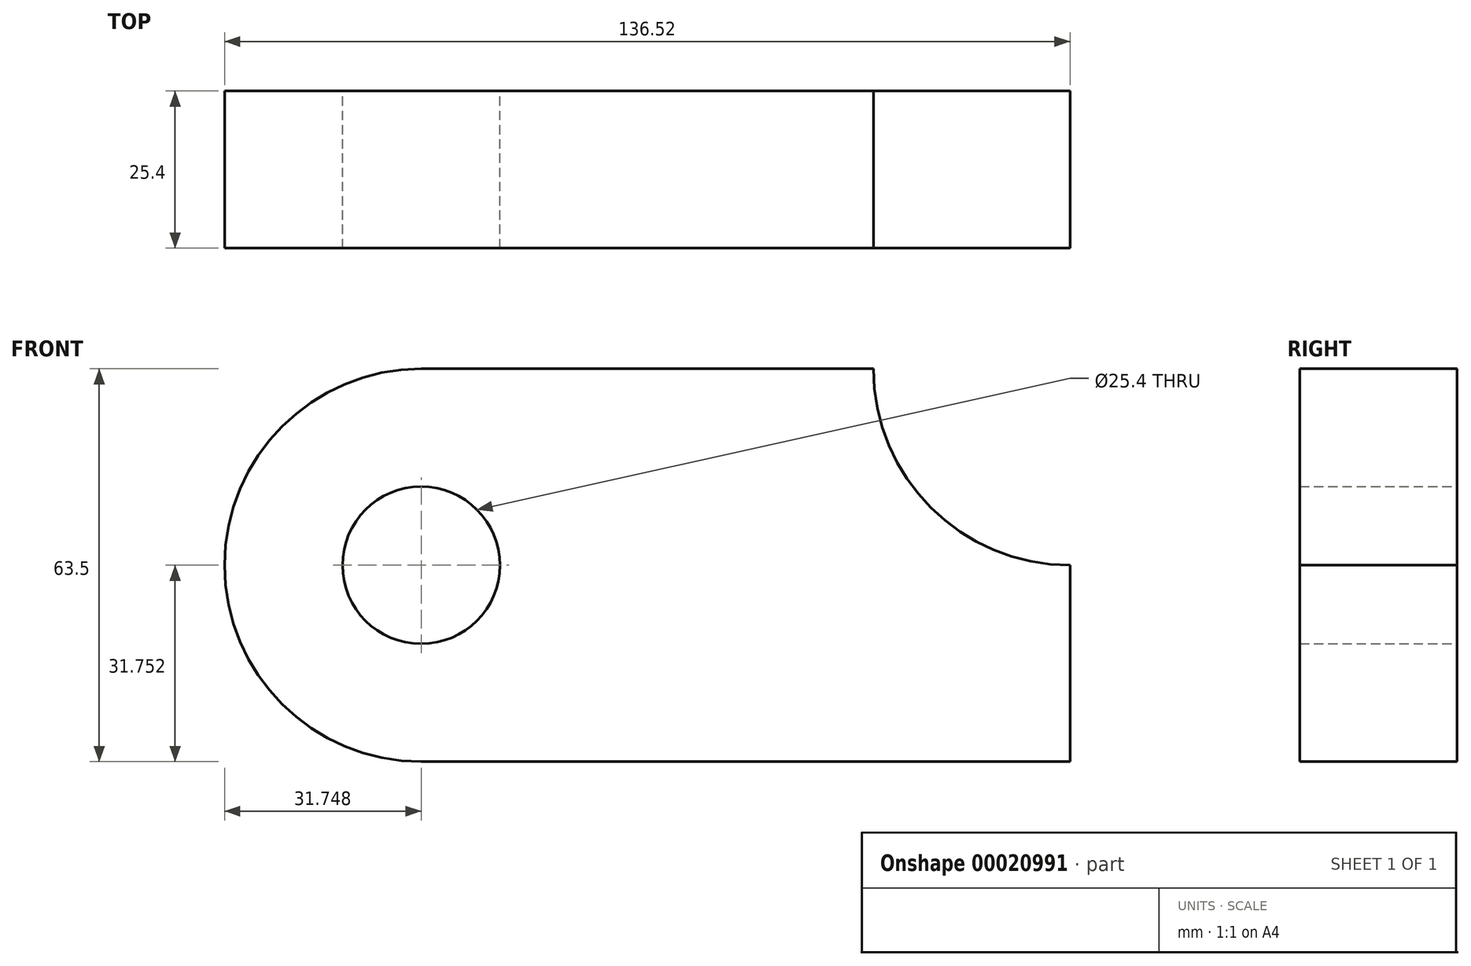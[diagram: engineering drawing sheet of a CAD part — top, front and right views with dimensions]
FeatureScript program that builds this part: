
annotation { "Feature Type Name" : "Feature", "Feature Type Description" : "" }
export const myFeature = defineFeature(function(context is Context, id is Id, definition is map)
    precondition{}
    {
        {
            var Q0;
            Q0=qCreatedBy(makeId("Front.planeOp"),FACE);
            var sketch = newSketch(context, id + "F0", { "sketchPlane" : qUnion([Q0])});
            skLineSegment(sketch, "E0.bottom", {"start": v(-39.55, 26.98) * mm, "end": v(33.47, 26.98) * mm});
            skLineSegment(sketch, "E0.top", {"start": v(-39.55, -36.52) * mm, "end": v(65.22, -36.52) * mm});
            skLineSegment(sketch, "E0.right", {"start": v(65.22, -4.77) * mm, "end": v(65.22, -36.52) * mm});
            skCircle(sketch, "E1", {"center": v(-39.55, -4.77) * mm, "radius": 31.75 * mm});
            skCircle(sketch, "E2", {"center": v(-39.55, -4.77) * mm, "radius": 12.7 * mm});
            skArc(sketch, "E3", {"start": v(33.47, 26.98) * mm, "mid": v(42.77, 4.53) * mm, "end": v(65.22, -4.77) * mm});
            skSolve(sketch);
        }
        {
            var Q0;
            Q0=makeQuery(id+"F0.imprint","IMPRINT",FACE,{"disambiguationData":[TD([[makeQuery(id+"F0.imprint","IMPRINT",EDGE,{"derivedFrom":sQuery(id+"F0.wireOp",EDGE,"E2")}),-1.0]])]});
            var Q1;
            {var subQ2=sQuery(id+"F0.wireOp",EDGE,"E0.bottom");Q1=makeQuery(id+"F0.imprint","IMPRINT",FACE,{"disambiguationData":[TD([[makeQuery(id+"F0.imprint","IMPRINT",EDGE,{"derivedFrom":subQ2}),-1.0]])]});}
            extrude(context, id + "F1", {"entities" : qUnion([Q0, Q1]), "depth" : 25.4 * mm});
        }
    });
